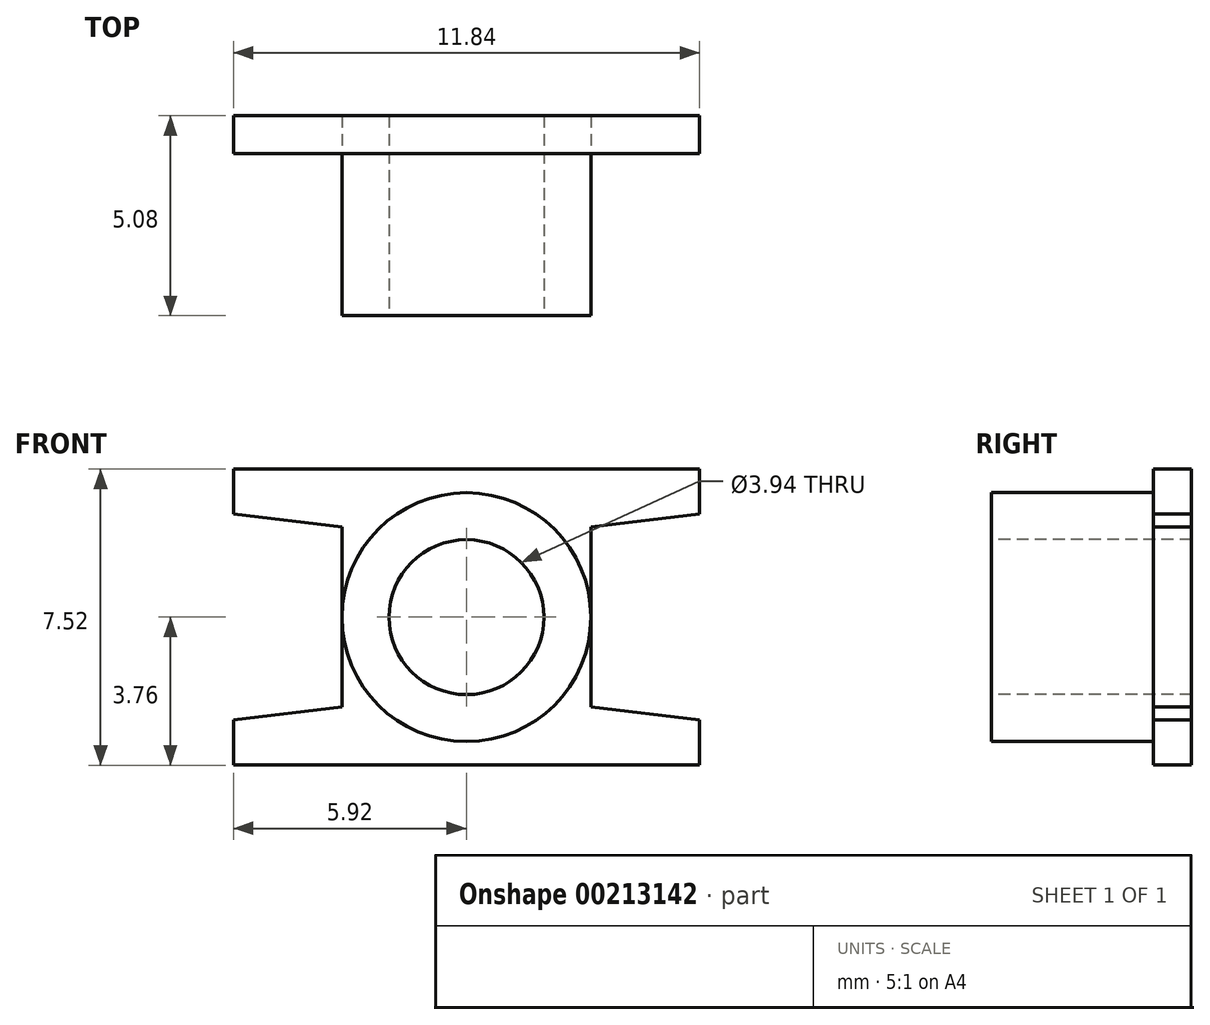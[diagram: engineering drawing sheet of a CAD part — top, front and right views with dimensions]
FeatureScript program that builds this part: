
annotation { "Feature Type Name" : "Feature", "Feature Type Description" : "" }
export const myFeature = defineFeature(function(context is Context, id is Id, definition is map)
    precondition{}
    {
        {
            var Q0;
            Q0=qCreatedBy(makeId("Front.planeOp"),FACE);
            var sketch = newSketch(context, id + "F0", { "sketchPlane" : qUnion([Q0])});
            skLineSegment(sketch, "E0.bottom", {"start": v(5.92, -3.76) * mm, "end": v(-5.92, -3.76) * mm});
            skLineSegment(sketch, "E0.top", {"start": v(5.92, 3.76) * mm, "end": v(-5.92, 3.76) * mm});
            skLineSegment(sketch, "E0.left", {"start": v(5.92, -3.76) * mm, "end": v(5.92, 3.76) * mm});
            skLineSegment(sketch, "E0.right", {"start": v(-5.92, -3.76) * mm, "end": v(-5.92, 3.76) * mm});
            skPoint(sketch, "E0.middle", {"position": v(0, 0) * mm});
            skSolve(sketch);
        }
        {
            var Q0;
            Q0=makeQuery(id+"F0.imprint","IMPRINT",FACE,{"disambiguationData":[TD([[makeQuery(id+"F0.imprint","IMPRINT",EDGE,{"derivedFrom":sQuery(id+"F0.wireOp",EDGE,"E0.bottom")}),-1.0]])]});
            extrude(context, id + "F1", {"entities" : qUnion([Q0]), "depth" : 0.97 * mm});
        }
        {
            var Q0;
            Q0=makeQuery(id+"F1.opExtrude","CAP_FACE",FACE,{"disambiguationData":[OSD([sQuery(id+"F0.wireOp",EDGE,"E0.bottom"),sQuery(id+"F0.wireOp",EDGE,"E0.top"),sQuery(id+"F0.wireOp",EDGE,"E0.left"),sQuery(id+"F0.wireOp",EDGE,"E0.right")])],"isStart":false});
            var sketch = newSketch(context, id + "F2", { "sketchPlane" : qUnion([Q0])});
            skCircle(sketch, "E1", {"center": v(0, 0) * mm, "radius": 3.16 * mm});
            skSolve(sketch);
        }
        {
            var Q0;
            Q0=makeQuery(id+"F2.imprint","IMPRINT",FACE,{"disambiguationData":[TD([[makeQuery(id+"F2.imprint","IMPRINT",EDGE,{"derivedFrom":sQuery(id+"F2.wireOp",EDGE,"E1")}),1.0]])]});
            extrude(context, id + "F3", {"entities" : qUnion([Q0]), "operationType" : NewBodyOperationType.ADD, "depth" : 4.11 * mm});
        }
        {
            var Q0;
            Q0=makeQuery(id+"F3.opExtrude","CAP_FACE",FACE,{"disambiguationData":[OSD([sQuery(id+"F2.wireOp",EDGE,"E1")])],"isStart":false});
            var sketch = newSketch(context, id + "F4", { "sketchPlane" : qUnion([Q0])});
            skCircle(sketch, "E2", {"center": v(0, 0) * mm, "radius": 1.97 * mm});
            skSolve(sketch);
        }
        {
            var Q0;
            Q0=makeQuery(id+"F4.imprint","IMPRINT",FACE,{"disambiguationData":[TD([[makeQuery(id+"F4.imprint","IMPRINT",EDGE,{"derivedFrom":sQuery(id+"F4.wireOp",EDGE,"E2")}),1.0]])]});
            extrude(context, id + "F5", {"entities" : qUnion([Q0]), "operationType" : NewBodyOperationType.REMOVE, "endBound" : BoundingType.THROUGH_ALL, "oppositeDirection" : true, "depth" : 25.4 * mm});
        }
        {
            var Q0;
            Q0=makeQuery(id+"F1.opExtrude","CAP_FACE",FACE,{"disambiguationData":[OSD([sQuery(id+"F0.wireOp",EDGE,"E0.bottom"),sQuery(id+"F0.wireOp",EDGE,"E0.top"),sQuery(id+"F0.wireOp",EDGE,"E0.left"),sQuery(id+"F0.wireOp",EDGE,"E0.right")])],"isStart":false});
            var sketch = newSketch(context, id + "F6", { "sketchPlane" : qUnion([Q0])});
            skLineSegment(sketch, "E3", {"start": v(-3.16, 0) * mm, "end": v(-3.16, 2.29) * mm});
            skLineSegment(sketch, "E4", {"start": v(-3.16, 0) * mm, "end": v(-3.16, -2.29) * mm});
            skLineSegment(sketch, "E5", {"start": v(-5.92, 3.76) * mm, "end": v(-5.92, 2.62) * mm});
            skLineSegment(sketch, "E6", {"start": v(-5.92, 2.62) * mm, "end": v(-3.16, 2.29) * mm});
            skLineSegment(sketch, "E7", {"start": v(-5.92, -3.76) * mm, "end": v(-5.92, -2.62) * mm});
            skLineSegment(sketch, "E8", {"start": v(-5.92, -2.62) * mm, "end": v(-3.16, -2.29) * mm});
            skLineSegment(sketch, "E9", {"start": v(3.16, 0) * mm, "end": v(3.16, 2.29) * mm});
            skLineSegment(sketch, "E10", {"start": v(3.16, 0) * mm, "end": v(3.16, -2.29) * mm});
            skLineSegment(sketch, "E11", {"start": v(5.92, 2.62) * mm, "end": v(3.16, 2.29) * mm});
            skLineSegment(sketch, "E12", {"start": v(5.92, -2.62) * mm, "end": v(3.16, -2.29) * mm});
            skSolve(sketch);
        }
        {
            var Q0;
            Q0=makeQuery(id+"F6.imprint","IMPRINT",FACE,{"disambiguationData":[TD([[makeQuery(id+"F6.imprint","IMPRINT",EDGE,{"derivedFrom":sQuery(id+"F6.wireOp",EDGE,"E3")}),1.0]])]});
            var Q1;
            Q1=makeQuery(id+"F6.imprint","IMPRINT",FACE,{"disambiguationData":[TD([[makeQuery(id+"F6.imprint","IMPRINT",EDGE,{"derivedFrom":sQuery(id+"F6.wireOp",EDGE,"E9")}),-1.0]])]});
            extrude(context, id + "F7", {"entities" : qUnion([Q0, Q1]), "operationType" : NewBodyOperationType.REMOVE, "endBound" : BoundingType.THROUGH_ALL, "oppositeDirection" : true, "depth" : 25.4 * mm});
        }
    });
